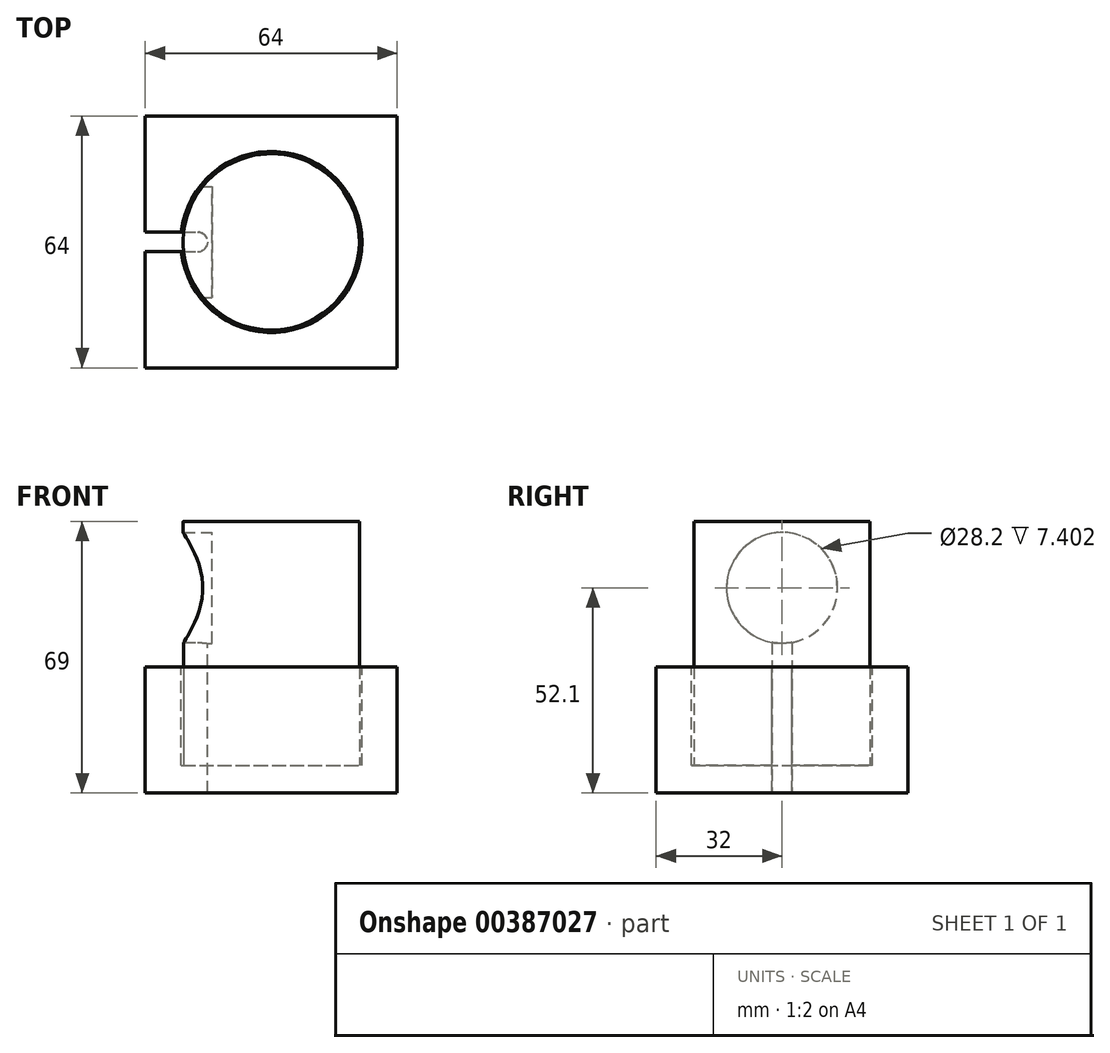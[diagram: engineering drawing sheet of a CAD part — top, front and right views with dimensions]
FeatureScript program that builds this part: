
annotation { "Feature Type Name" : "Feature", "Feature Type Description" : "" }
export const myFeature = defineFeature(function(context is Context, id is Id, definition is map)
    precondition{}
    {
        {
            var Q0;
            Q0=qCreatedBy(makeId("Top.planeOp"),FACE);
            var sketch = newSketch(context, id + "F0", { "sketchPlane" : qUnion([Q0])});
            skLineSegment(sketch, "E0.bottom", {"start": v(32, -32) * mm, "end": v(-32, -32) * mm});
            skLineSegment(sketch, "E0.top", {"start": v(32, 32) * mm, "end": v(-32, 32) * mm});
            skLineSegment(sketch, "E0.left", {"start": v(32, -32) * mm, "end": v(32, 32) * mm});
            skLineSegment(sketch, "E0.right", {"start": v(-32, -32) * mm, "end": v(-32, 32) * mm});
            skPoint(sketch, "E0.middle", {"position": v(0, 0) * mm});
            skSolve(sketch);
        }
        {
            var Q0;
            Q0 = qSketchRegion(id + "F0", true);
            extrude(context, id + "F1", {"entities" : qUnion([Q0]), "depth" : 32 * mm});
        }
        {
            var Q0;
            Q0=makeQuery(id+"F1.opExtrude","CAP_FACE",FACE,{"disambiguationData":[OSD([sQuery(id+"F0.wireOp",EDGE,"E0.bottom"),sQuery(id+"F0.wireOp",EDGE,"E0.top"),sQuery(id+"F0.wireOp",EDGE,"E0.left"),sQuery(id+"F0.wireOp",EDGE,"E0.right")])],"isStart":false});
            var sketch = newSketch(context, id + "F2", { "sketchPlane" : qUnion([Q0])});
            skCircle(sketch, "E1", {"center": v(0, 0) * mm, "radius": 23 * mm});
            skSolve(sketch);
        }
        {
            var Q0;
            Q0 = qSketchRegion(id + "F2", true);
            extrude(context, id + "F3", {"entities" : qUnion([Q0]), "operationType" : NewBodyOperationType.REMOVE, "oppositeDirection" : true, "depth" : 25 * mm});
        }
        {
            var Q0;
            Q0=makeQuery(id+"F3.boolean.opBoolean","COPY",FACE,{"derivedFrom":makeQuery(id+"F3.opExtrude","CAP_FACE",FACE,{"disambiguationData":[OSD([sQuery(id+"F2.wireOp",EDGE,"E1")])],"isStart":false})});
            var sketch = newSketch(context, id + "F4", { "sketchPlane" : qUnion([Q0])});
            skSolve(sketch);
        }
        {
            var Q0;
            Q0=makeQuery(id+"F4.imprint","IMPRINT",FACE,{"disambiguationData":[TD([[makeQuery(id+"F4.imprint","IMPRINT",EDGE,{"derivedFrom":makeQuery(id+"F3.boolean.opBoolean","COPY",EDGE,{"derivedFrom":makeQuery(id+"F3.opExtrude","CAP_EDGE",EDGE,{"disambiguationData":[OSD([sQuery(id+"F2.wireOp",EDGE,"E1")])],"isStart":false})})}),1.0]])]});
            var sketch = newSketch(context, id + "F5", { "sketchPlane" : qUnion([Q0])});
            skCircle(sketch, "E2", {"center": v(0, 0) * mm, "radius": 22.4 * mm});
            skSolve(sketch);
        }
        {
            var Q0;
            Q0 = qSketchRegion(id + "F5", true);
            extrude(context, id + "F6", {"entities" : qUnion([Q0]), "depth" : 62 * mm});
        }
        {
            var Q0;
            Q0=qCreatedBy(makeId("Right.planeOp"),FACE);
            var sketch = newSketch(context, id + "F7", { "sketchPlane" : qUnion([Q0])});
            skCircle(sketch, "E3", {"center": v(0, 52.1) * mm, "radius": 14.1 * mm});
            skSolve(sketch);
        }
        {
            var Q0;
            Q0 = qSketchRegion(id + "F7", true);
            extrude(context, id + "F8", {"entities" : qUnion([Q0]), "operationType" : NewBodyOperationType.REMOVE, "oppositeDirection" : true, "depth" : 37.8 * mm, "hasSecondDirection" : true, "secondDirectionOppositeDirection" : true, "secondDirectionDepth" : 15 * mm});
        }
        {
            var Q0;
            Q0=makeQuery(id+"F8.boolean.opBoolean","COPY",FACE,{"derivedFrom":makeQuery(id+"F8.opExtrude","CAP_FACE",FACE,{"disambiguationData":[OSD([sQuery(id+"F7.wireOp",EDGE,"E3")])],"isStart":true})});
            var sketch = newSketch(context, id + "F9", { "sketchPlane" : qUnion([Q0])});
            skLineSegment(sketch, "E4.bottom", {"start": v(2.5, 43.35) * mm, "end": v(-2.5, 43.35) * mm});
            skLineSegment(sketch, "E4.top", {"start": v(2.5, -43.35) * mm, "end": v(-2.5, -43.35) * mm});
            skLineSegment(sketch, "E4.left", {"start": v(2.5, 43.35) * mm, "end": v(2.5, -43.35) * mm});
            skLineSegment(sketch, "E4.right", {"start": v(-2.5, 43.35) * mm, "end": v(-2.5, -43.35) * mm});
            skPoint(sketch, "E4.middle", {"position": v(0, 0) * mm});
            skSolve(sketch);
        }
        {
            var Q0;
            Q0 = qSketchRegion(id + "F9", true);
            extrude(context, id + "F10", {"entities" : qUnion([Q0]), "operationType" : NewBodyOperationType.REMOVE, "depth" : 25 * mm, "hasSecondDirection" : true, "secondDirectionOppositeDirection" : false, "secondDirectionDepth" : 1.2 * mm});
        }
        {
            var Q0;
            Q0=makeQuery(id+"F10.boolean.opBoolean","COPY",EDGE,{"derivedFrom":makeQuery(id+"F10.opExtrude","CAP_EDGE",EDGE,{"disambiguationData":[OSD([sQuery(id+"F9.wireOp",EDGE,"E4.right")])],"isStart":true})});
            var Q1;
            Q1=makeQuery(id+"F10.boolean.opBoolean","COPY",EDGE,{"derivedFrom":makeQuery(id+"F10.opExtrude","CAP_EDGE",EDGE,{"disambiguationData":[OSD([sQuery(id+"F9.wireOp",EDGE,"E4.left")])],"isStart":true})});
            fillet(context, id + "F11", {"entities" : qUnion([Q0, Q1]), "radius" : 2.5 * mm, "tangentPropagation" : true, "allowEdgeOverflow" : false});
        }
        {
            var Q0;
            Q0=makeQuery(id+"F4.imprint","IMPRINT",FACE,{"disambiguationData":[TD([[makeQuery(id+"F4.imprint","IMPRINT",EDGE,{"derivedFrom":makeQuery(id+"F3.boolean.opBoolean","COPY",EDGE,{"derivedFrom":makeQuery(id+"F3.opExtrude","CAP_EDGE",EDGE,{"disambiguationData":[OSD([sQuery(id+"F2.wireOp",EDGE,"E1")])],"isStart":false})})}),1.0]])]});
            var sketch = newSketch(context, id + "F12", { "sketchPlane" : qUnion([Q0])});
            skCircle(sketch, "E5.cCircle", {"center": v(0, 0) * mm, "radius": 11 * mm, "construction": true});
            skLineSegment(sketch, "E5.0", {"start": v(11, 4.56) * mm, "end": v(11, -4.56) * mm});
            skLineSegment(sketch, "E5.1", {"start": v(11, -4.56) * mm, "end": v(4.56, -11) * mm});
            skLineSegment(sketch, "E5.2", {"start": v(4.56, -11) * mm, "end": v(-4.56, -11) * mm});
            skLineSegment(sketch, "E5.3", {"start": v(-4.56, -11) * mm, "end": v(-11, -4.56) * mm});
            skLineSegment(sketch, "E5.4", {"start": v(-11, -4.56) * mm, "end": v(-11, 4.56) * mm});
            skLineSegment(sketch, "E5.5", {"start": v(-11, 4.56) * mm, "end": v(-4.56, 11) * mm});
            skLineSegment(sketch, "E5.6", {"start": v(-4.56, 11) * mm, "end": v(4.56, 11) * mm});
            skLineSegment(sketch, "E5.7", {"start": v(4.56, 11) * mm, "end": v(11, 4.56) * mm});
            skPoint(sketch, "E5.0.midPoint", {"position": v(11, 0) * mm});
            skSolve(sketch);
        }
        {
            var Q0;
            Q0 = qSketchRegion(id + "F12", true);
            extrude(context, id + "F13", {"entities" : qUnion([Q0]), "operationType" : NewBodyOperationType.REMOVE, "depth" : 10 * mm});
        }
        {
            var Q0;
            Q0=makeQuery(id+"F4.imprint","IMPRINT",FACE,{"disambiguationData":[TD([[makeQuery(id+"F4.imprint","IMPRINT",EDGE,{"derivedFrom":makeQuery(id+"F3.boolean.opBoolean","COPY",EDGE,{"derivedFrom":makeQuery(id+"F3.opExtrude","CAP_EDGE",EDGE,{"disambiguationData":[OSD([sQuery(id+"F2.wireOp",EDGE,"E1")])],"isStart":false})})}),1.0]])]});
            var sketch = newSketch(context, id + "F14", { "sketchPlane" : qUnion([Q0])});
            skCircle(sketch, "E6.cCircle", {"center": v(0, 0) * mm, "radius": 12.5 * mm, "construction": true});
            skLineSegment(sketch, "E6.0", {"start": v(-5.18, 12.5) * mm, "end": v(5.18, 12.5) * mm});
            skLineSegment(sketch, "E6.1", {"start": v(5.18, 12.5) * mm, "end": v(12.5, 5.18) * mm});
            skLineSegment(sketch, "E6.2", {"start": v(12.5, 5.18) * mm, "end": v(12.5, -5.18) * mm});
            skLineSegment(sketch, "E6.3", {"start": v(12.5, -5.18) * mm, "end": v(5.18, -12.5) * mm});
            skLineSegment(sketch, "E6.4", {"start": v(5.18, -12.5) * mm, "end": v(-5.18, -12.5) * mm});
            skLineSegment(sketch, "E6.5", {"start": v(-5.18, -12.5) * mm, "end": v(-12.5, -5.18) * mm});
            skLineSegment(sketch, "E6.6", {"start": v(-12.5, -5.18) * mm, "end": v(-12.5, 5.18) * mm});
            skLineSegment(sketch, "E6.7", {"start": v(-12.5, 5.18) * mm, "end": v(-5.18, 12.5) * mm});
            skPoint(sketch, "E6.0.midPoint", {"position": v(0, 12.5) * mm});
            skSolve(sketch);
        }
        {
            var Q0;
            Q0 = qSketchRegion(id + "F14", true);
            extrude(context, id + "F15", {"entities" : qUnion([Q0]), "operationType" : NewBodyOperationType.ADD, "depth" : 10 * mm});
        }
    });
